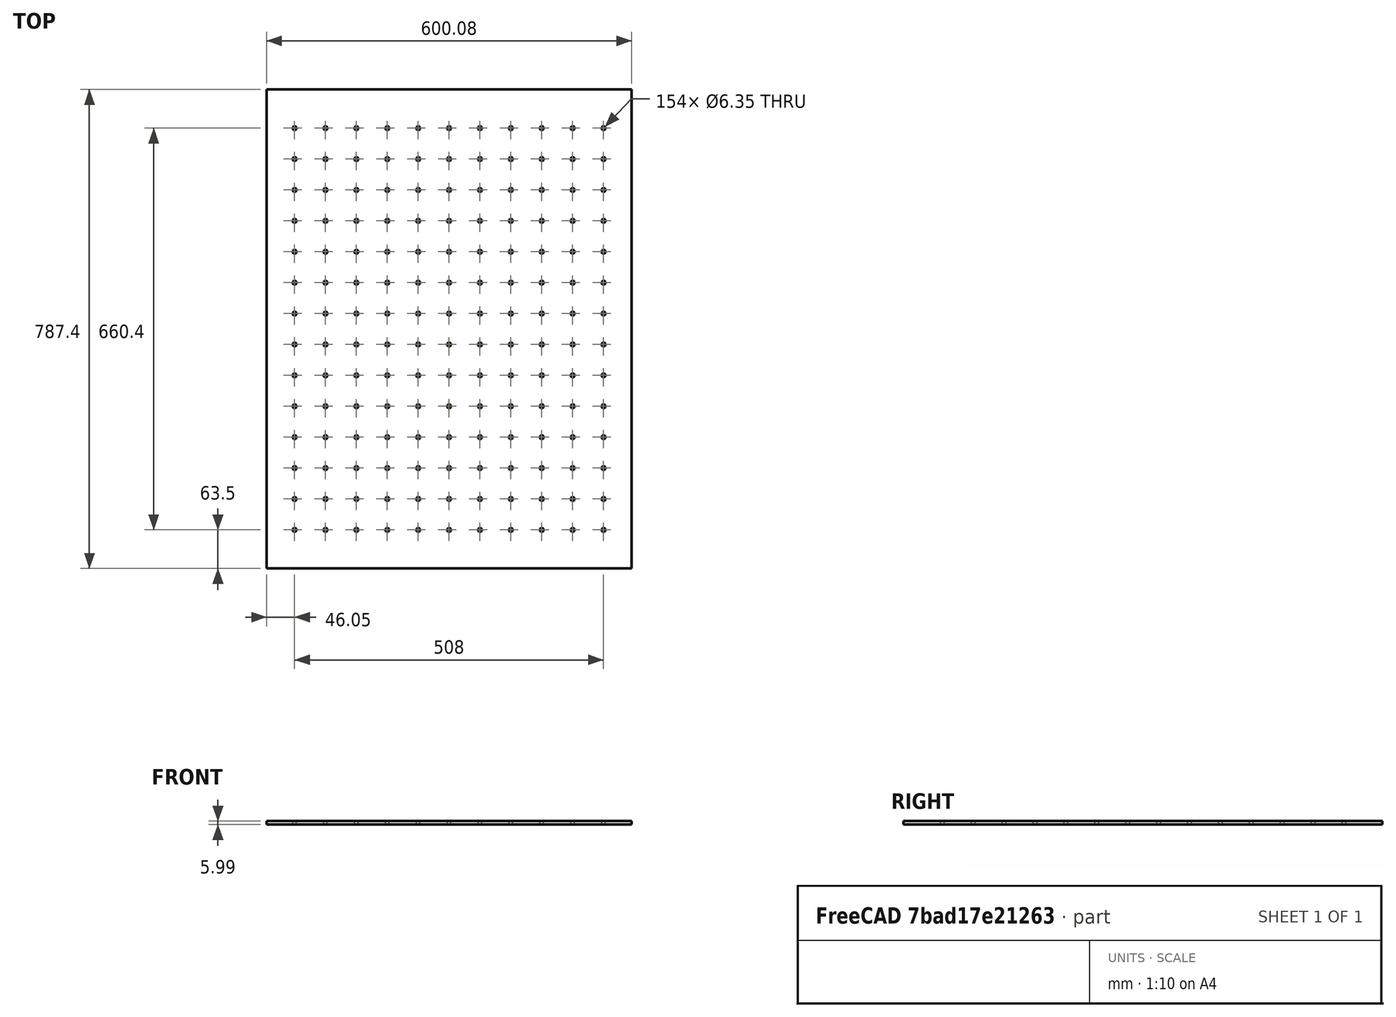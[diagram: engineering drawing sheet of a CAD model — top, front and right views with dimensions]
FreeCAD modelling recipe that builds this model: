
FCSTD DOCUMENT  (FreeCAD 0.19R24267 (Git))
Label: Inv2-P6
License: All rights reserved
LicenseURL: http://en.wikipedia.org/wiki/All_rights_reserved
objects: TechDraw::DrawViewDimension×8, TechDraw::DrawViewAnnotation×3, TechDraw::DrawProjGroupItem×2, TechDraw::DrawHatch×2, Sketcher::SketchObject×1, Part::Extrusion×1, TechDraw::DrawSVGTemplate×1, TechDraw::DrawProjGroup×1, TechDraw::DrawPage×1
note: 2 computed .brp shape members not serialized (recipe doc carries the construction recipe); baked Part::Feature solids carry a one-line shape summary decoded from their .brp

FEATURE [Sketcher::SketchObject] Sketch
  FullyConstrained = true
  sketch-geometry (311):
    g0: LineSegment StartX=0 StartY=0 StartZ=0 EndX=600.075 EndY=0 EndZ=0
    g1: LineSegment StartX=600.075 StartY=0 StartZ=0 EndX=600.075 EndY=-787.4 EndZ=0
    g2: LineSegment StartX=600.075 StartY=-787.4 StartZ=0 EndX=0 EndY=-787.4 EndZ=0
    g3: LineSegment StartX=0 StartY=-787.4 StartZ=0 EndX=0 EndY=0 EndZ=0
    g4: Circle CenterX=46.0502 CenterY=-63.5 CenterZ=0 NormalX=0 NormalY=0 NormalZ=1 AngleXU=0 Radius=3.175
    g5: Circle CenterX=96.8502 CenterY=-63.5 CenterZ=0 NormalX=0 NormalY=0 NormalZ=1 AngleXU=0 Radius=3.175
    g6: LineSegment StartX=46.0502 StartY=-63.5 StartZ=0 EndX=96.8502 EndY=-63.5 EndZ=0
    g7: Circle CenterX=147.65 CenterY=-63.5 CenterZ=0 NormalX=0 NormalY=0 NormalZ=1 AngleXU=0 Radius=3.175
    g8: LineSegment StartX=96.8502 StartY=-63.5 StartZ=0 EndX=147.65 EndY=-63.5 EndZ=0
    g9: Circle CenterX=198.45 CenterY=-63.5 CenterZ=0 NormalX=0 NormalY=0 NormalZ=1 AngleXU=0 Radius=3.175
    g10: LineSegment StartX=147.65 StartY=-63.5 StartZ=0 EndX=198.45 EndY=-63.5 EndZ=0
    g11: Circle CenterX=249.25 CenterY=-63.5 CenterZ=0 NormalX=0 NormalY=0 NormalZ=1 AngleXU=0 Radius=3.175
    g12: LineSegment StartX=198.45 StartY=-63.5 StartZ=0 EndX=249.25 EndY=-63.5 EndZ=0
    g13: Circle CenterX=300.05 CenterY=-63.5 CenterZ=0 NormalX=0 NormalY=0 NormalZ=1 AngleXU=0 Radius=3.175
    g14: LineSegment StartX=249.25 StartY=-63.5 StartZ=0 EndX=300.05 EndY=-63.5 EndZ=0
    g15: Circle CenterX=350.85 CenterY=-63.5 CenterZ=0 NormalX=0 NormalY=0 NormalZ=1 AngleXU=0 Radius=3.175
    g16: LineSegment StartX=300.05 StartY=-63.5 StartZ=0 EndX=350.85 EndY=-63.5 EndZ=0
    g17: Circle CenterX=401.65 CenterY=-63.5 CenterZ=0 NormalX=0 NormalY=0 NormalZ=1 AngleXU=0 Radius=3.175
    g18: LineSegment StartX=350.85 StartY=-63.5 StartZ=0 EndX=401.65 EndY=-63.5 EndZ=0
    g19: Circle CenterX=452.45 CenterY=-63.5 CenterZ=0 NormalX=0 NormalY=0 NormalZ=1 AngleXU=0 Radius=3.175
    g20: LineSegment StartX=401.65 StartY=-63.5 StartZ=0 EndX=452.45 EndY=-63.5 EndZ=0
    g21: Circle CenterX=503.25 CenterY=-63.5 CenterZ=0 NormalX=0 NormalY=0 NormalZ=1 AngleXU=0 Radius=3.175
    g22: LineSegment StartX=452.45 StartY=-63.5 StartZ=0 EndX=503.25 EndY=-63.5 EndZ=0
    g23: Circle CenterX=554.05 CenterY=-63.5 CenterZ=0 NormalX=0 NormalY=0 NormalZ=1 AngleXU=0 Radius=3.175
    g24: LineSegment StartX=503.25 StartY=-63.5 StartZ=0 EndX=554.05 EndY=-63.5 EndZ=0
    g25: Circle CenterX=46.0502 CenterY=-114.3 CenterZ=0 NormalX=0 NormalY=0 NormalZ=1 AngleXU=0 Radius=3.175
    g26: LineSegment StartX=46.0502 StartY=-63.5 StartZ=0 EndX=46.0502 EndY=-114.3 EndZ=0
    g27: Circle CenterX=96.8502 CenterY=-114.3 CenterZ=0 NormalX=0 NormalY=0 NormalZ=1 AngleXU=0 Radius=3.175
    g28: LineSegment StartX=46.0502 StartY=-114.3 StartZ=0 EndX=96.8502 EndY=-114.3 EndZ=0
    g29: Circle CenterX=147.65 CenterY=-114.3 CenterZ=0 NormalX=0 NormalY=0 NormalZ=1 AngleXU=0 Radius=3.175
    g30: LineSegment StartX=96.8502 StartY=-114.3 StartZ=0 EndX=147.65 EndY=-114.3 EndZ=0
    g31: Circle CenterX=198.45 CenterY=-114.3 CenterZ=0 NormalX=0 NormalY=0 NormalZ=1 AngleXU=0 Radius=3.175
    g32: LineSegment StartX=147.65 StartY=-114.3 StartZ=0 EndX=198.45 EndY=-114.3 EndZ=0
    g33: Circle CenterX=249.25 CenterY=-114.3 CenterZ=0 NormalX=0 NormalY=0 NormalZ=1 AngleXU=0 Radius=3.175
    g34: LineSegment StartX=198.45 StartY=-114.3 StartZ=0 EndX=249.25 EndY=-114.3 EndZ=0
    g35: Circle CenterX=300.05 CenterY=-114.3 CenterZ=0 NormalX=0 NormalY=0 NormalZ=1 AngleXU=0 Radius=3.175
    g36: LineSegment StartX=249.25 StartY=-114.3 StartZ=0 EndX=300.05 EndY=-114.3 EndZ=0
    g37: Circle CenterX=350.85 CenterY=-114.3 CenterZ=0 NormalX=0 NormalY=0 NormalZ=1 AngleXU=0 Radius=3.175
    g38: LineSegment StartX=300.05 StartY=-114.3 StartZ=0 EndX=350.85 EndY=-114.3 EndZ=0
    g39: Circle CenterX=401.65 CenterY=-114.3 CenterZ=0 NormalX=0 NormalY=0 NormalZ=1 AngleXU=0 Radius=3.175
    g40: LineSegment StartX=350.85 StartY=-114.3 StartZ=0 EndX=401.65 EndY=-114.3 EndZ=0
    g41: Circle CenterX=452.45 CenterY=-114.3 CenterZ=0 NormalX=0 NormalY=0 NormalZ=1 AngleXU=0 Radius=3.175
    g42: LineSegment StartX=401.65 StartY=-114.3 StartZ=0 EndX=452.45 EndY=-114.3 EndZ=0
    g43: Circle CenterX=503.25 CenterY=-114.3 CenterZ=0 NormalX=0 NormalY=0 NormalZ=1 AngleXU=0 Radius=3.175
    g44: LineSegment StartX=452.45 StartY=-114.3 StartZ=0 EndX=503.25 EndY=-114.3 EndZ=0
    g45: Circle CenterX=554.05 CenterY=-114.3 CenterZ=0 NormalX=0 NormalY=0 NormalZ=1 AngleXU=0 Radius=3.175
    g46: LineSegment StartX=503.25 StartY=-114.3 StartZ=0 EndX=554.05 EndY=-114.3 EndZ=0
    g47: Circle CenterX=46.0502 CenterY=-165.1 CenterZ=0 NormalX=0 NormalY=0 NormalZ=1 AngleXU=0 Radius=3.175
    g48: LineSegment StartX=46.0502 StartY=-114.3 StartZ=0 EndX=46.0502 EndY=-165.1 EndZ=0
    g49: Circle CenterX=96.8502 CenterY=-165.1 CenterZ=0 NormalX=0 NormalY=0 NormalZ=1 AngleXU=0 Radius=3.175
    g50: LineSegment StartX=46.0502 StartY=-165.1 StartZ=0 EndX=96.8502 EndY=-165.1 EndZ=0
    g51: Circle CenterX=147.65 CenterY=-165.1 CenterZ=0 NormalX=0 NormalY=0 NormalZ=1 AngleXU=0 Radius=3.175
    g52: LineSegment StartX=96.8502 StartY=-165.1 StartZ=0 EndX=147.65 EndY=-165.1 EndZ=0
    g53: Circle CenterX=198.45 CenterY=-165.1 CenterZ=0 NormalX=0 NormalY=0 NormalZ=1 AngleXU=0 Radius=3.175
    g54: LineSegment StartX=147.65 StartY=-165.1 StartZ=0 EndX=198.45 EndY=-165.1 EndZ=0
    g55: Circle CenterX=249.25 CenterY=-165.1 CenterZ=0 NormalX=0 NormalY=0 NormalZ=1 AngleXU=0 Radius=3.175
    g56: LineSegment StartX=198.45 StartY=-165.1 StartZ=0 EndX=249.25 EndY=-165.1 EndZ=0
    g57: Circle CenterX=300.05 CenterY=-165.1 CenterZ=0 NormalX=0 NormalY=0 NormalZ=1 AngleXU=0 Radius=3.175
    g58: LineSegment StartX=249.25 StartY=-165.1 StartZ=0 EndX=300.05 EndY=-165.1 EndZ=0
    g59: Circle CenterX=350.85 CenterY=-165.1 CenterZ=0 NormalX=0 NormalY=0 NormalZ=1 AngleXU=0 Radius=3.175
    g60: LineSegment StartX=300.05 StartY=-165.1 StartZ=0 EndX=350.85 EndY=-165.1 EndZ=0
    g61: Circle CenterX=401.65 CenterY=-165.1 CenterZ=0 NormalX=0 NormalY=0 NormalZ=1 AngleXU=0 Radius=3.175
    g62: LineSegment StartX=350.85 StartY=-165.1 StartZ=0 EndX=401.65 EndY=-165.1 EndZ=0
    g63: Circle CenterX=452.45 CenterY=-165.1 CenterZ=0 NormalX=0 NormalY=0 NormalZ=1 AngleXU=0 Radius=3.175
    g64: LineSegment StartX=401.65 StartY=-165.1 StartZ=0 EndX=452.45 EndY=-165.1 EndZ=0
    g65: Circle CenterX=503.25 CenterY=-165.1 CenterZ=0 NormalX=0 NormalY=0 NormalZ=1 AngleXU=0 Radius=3.175
    g66: LineSegment StartX=452.45 StartY=-165.1 StartZ=0 EndX=503.25 EndY=-165.1 EndZ=0
    g67: Circle CenterX=554.05 CenterY=-165.1 CenterZ=0 NormalX=0 NormalY=0 NormalZ=1 AngleXU=0 Radius=3.175
    g68: LineSegment StartX=503.25 StartY=-165.1 StartZ=0 EndX=554.05 EndY=-165.1 EndZ=0
    g69: Circle CenterX=46.0502 CenterY=-215.9 CenterZ=0 NormalX=0 NormalY=0 NormalZ=1 AngleXU=0 Radius=3.175
    g70: LineSegment StartX=46.0502 StartY=-165.1 StartZ=0 EndX=46.0502 EndY=-215.9 EndZ=0
    g71: Circle CenterX=96.8502 CenterY=-215.9 CenterZ=0 NormalX=0 NormalY=0 NormalZ=1 AngleXU=0 Radius=3.175
    g72: LineSegment StartX=46.0502 StartY=-215.9 StartZ=0 EndX=96.8502 EndY=-215.9 EndZ=0
    g73: Circle CenterX=147.65 CenterY=-215.9 CenterZ=0 NormalX=0 NormalY=0 NormalZ=1 AngleXU=0 Radius=3.175
    g74: LineSegment StartX=96.8502 StartY=-215.9 StartZ=0 EndX=147.65 EndY=-215.9 EndZ=0
    g75: Circle CenterX=198.45 CenterY=-215.9 CenterZ=0 NormalX=0 NormalY=0 NormalZ=1 AngleXU=0 Radius=3.175
    g76: LineSegment StartX=147.65 StartY=-215.9 StartZ=0 EndX=198.45 EndY=-215.9 EndZ=0
    g77: Circle CenterX=249.25 CenterY=-215.9 CenterZ=0 NormalX=0 NormalY=0 NormalZ=1 AngleXU=0 Radius=3.175
    g78: LineSegment StartX=198.45 StartY=-215.9 StartZ=0 EndX=249.25 EndY=-215.9 EndZ=0
    g79: Circle CenterX=300.05 CenterY=-215.9 CenterZ=0 NormalX=0 NormalY=0 NormalZ=1 AngleXU=0 Radius=3.175
    g80: LineSegment StartX=249.25 StartY=-215.9 StartZ=0 EndX=300.05 EndY=-215.9 EndZ=0
    g81: Circle CenterX=350.85 CenterY=-215.9 CenterZ=0 NormalX=0 NormalY=0 NormalZ=1 AngleXU=0 Radius=3.175
    g82: LineSegment StartX=300.05 StartY=-215.9 StartZ=0 EndX=350.85 EndY=-215.9 EndZ=0
    g83: Circle CenterX=401.65 CenterY=-215.9 CenterZ=0 NormalX=0 NormalY=0 NormalZ=1 AngleXU=0 Radius=3.175
    g84: LineSegment StartX=350.85 StartY=-215.9 StartZ=0 EndX=401.65 EndY=-215.9 EndZ=0
    g85: Circle CenterX=452.45 CenterY=-215.9 CenterZ=0 NormalX=0 NormalY=0 NormalZ=1 AngleXU=0 Radius=3.175
    g86: LineSegment StartX=401.65 StartY=-215.9 StartZ=0 EndX=452.45 EndY=-215.9 EndZ=0
    g87: Circle CenterX=503.25 CenterY=-215.9 CenterZ=0 NormalX=0 NormalY=0 NormalZ=1 AngleXU=0 Radius=3.175
    g88: LineSegment StartX=452.45 StartY=-215.9 StartZ=0 EndX=503.25 EndY=-215.9 EndZ=0
    g89: Circle CenterX=554.05 CenterY=-215.9 CenterZ=0 NormalX=0 NormalY=0 NormalZ=1 AngleXU=0 Radius=3.175
    g90: LineSegment StartX=503.25 StartY=-215.9 StartZ=0 EndX=554.05 EndY=-215.9 EndZ=0
    g91: Circle CenterX=46.0502 CenterY=-266.7 CenterZ=0 NormalX=0 NormalY=0 NormalZ=1 AngleXU=0 Radius=3.175
    g92: LineSegment StartX=46.0502 StartY=-215.9 StartZ=0 EndX=46.0502 EndY=-266.7 EndZ=0
    g93: Circle CenterX=96.8502 CenterY=-266.7 CenterZ=0 NormalX=0 NormalY=0 NormalZ=1 AngleXU=0 Radius=3.175
    g94: LineSegment StartX=46.0502 StartY=-266.7 StartZ=0 EndX=96.8502 EndY=-266.7 EndZ=0
    g95: Circle CenterX=147.65 CenterY=-266.7 CenterZ=0 NormalX=0 NormalY=0 NormalZ=1 AngleXU=0 Radius=3.175
    g96: LineSegment StartX=96.8502 StartY=-266.7 StartZ=0 EndX=147.65 EndY=-266.7 EndZ=0
    g97: Circle CenterX=198.45 CenterY=-266.7 CenterZ=0 NormalX=0 NormalY=0 NormalZ=1 AngleXU=0 Radius=3.175
    g98: LineSegment StartX=147.65 StartY=-266.7 StartZ=0 EndX=198.45 EndY=-266.7 EndZ=0
    g99: Circle CenterX=249.25 CenterY=-266.7 CenterZ=0 NormalX=0 NormalY=0 NormalZ=1 AngleXU=0 Radius=3.175
    g100: LineSegment StartX=198.45 StartY=-266.7 StartZ=0 EndX=249.25 EndY=-266.7 EndZ=0
    g101: Circle CenterX=300.05 CenterY=-266.7 CenterZ=0 NormalX=0 NormalY=0 NormalZ=1 AngleXU=0 Radius=3.175
    g102: LineSegment StartX=249.25 StartY=-266.7 StartZ=0 EndX=300.05 EndY=-266.7 EndZ=0
    g103: Circle CenterX=350.85 CenterY=-266.7 CenterZ=0 NormalX=0 NormalY=0 NormalZ=1 AngleXU=0 Radius=3.175
    g104: LineSegment StartX=300.05 StartY=-266.7 StartZ=0 EndX=350.85 EndY=-266.7 EndZ=0
    g105: Circle CenterX=401.65 CenterY=-266.7 CenterZ=0 NormalX=0 NormalY=0 NormalZ=1 AngleXU=0 Radius=3.175
    g106: LineSegment StartX=350.85 StartY=-266.7 StartZ=0 EndX=401.65 EndY=-266.7 EndZ=0
    g107: Circle CenterX=452.45 CenterY=-266.7 CenterZ=0 NormalX=0 NormalY=0 NormalZ=1 AngleXU=0 Radius=3.175
    g108: LineSegment StartX=401.65 StartY=-266.7 StartZ=0 EndX=452.45 EndY=-266.7 EndZ=0
    g109: Circle CenterX=503.25 CenterY=-266.7 CenterZ=0 NormalX=0 NormalY=0 NormalZ=1 AngleXU=0 Radius=3.175
    g110: LineSegment StartX=452.45 StartY=-266.7 StartZ=0 EndX=503.25 EndY=-266.7 EndZ=0
    g111: Circle CenterX=554.05 CenterY=-266.7 CenterZ=0 NormalX=0 NormalY=0 NormalZ=1 AngleXU=0 Radius=3.175
    g112: LineSegment StartX=503.25 StartY=-266.7 StartZ=0 EndX=554.05 EndY=-266.7 EndZ=0
    g113: Circle CenterX=46.0502 CenterY=-317.5 CenterZ=0 NormalX=0 NormalY=0 NormalZ=1 AngleXU=0 Radius=3.175
    g114: LineSegment StartX=46.0502 StartY=-266.7 StartZ=0 EndX=46.0502 EndY=-317.5 EndZ=0
    g115: Circle CenterX=96.8502 CenterY=-317.5 CenterZ=0 NormalX=0 NormalY=0 NormalZ=1 AngleXU=0 Radius=3.175
    g116: LineSegment StartX=46.0502 StartY=-317.5 StartZ=0 EndX=96.8502 EndY=-317.5 EndZ=0
    g117: Circle CenterX=147.65 CenterY=-317.5 CenterZ=0 NormalX=0 NormalY=0 NormalZ=1 AngleXU=0 Radius=3.175
    g118: LineSegment StartX=96.8502 StartY=-317.5 StartZ=0 EndX=147.65 EndY=-317.5 EndZ=0
    g119: Circle CenterX=198.45 CenterY=-317.5 CenterZ=0 NormalX=0 NormalY=0 NormalZ=1 AngleXU=0 Radius=3.175
    g120: LineSegment StartX=147.65 StartY=-317.5 StartZ=0 EndX=198.45 EndY=-317.5 EndZ=0
    g121: Circle CenterX=249.25 CenterY=-317.5 CenterZ=0 NormalX=0 NormalY=0 NormalZ=1 AngleXU=0 Radius=3.175
    g122: LineSegment StartX=198.45 StartY=-317.5 StartZ=0 EndX=249.25 EndY=-317.5 EndZ=0
    g123: Circle CenterX=300.05 CenterY=-317.5 CenterZ=0 NormalX=0 NormalY=0 NormalZ=1 AngleXU=0 Radius=3.175
    g124: LineSegment StartX=249.25 StartY=-317.5 StartZ=0 EndX=300.05 EndY=-317.5 EndZ=0
    g125: Circle CenterX=350.85 CenterY=-317.5 CenterZ=0 NormalX=0 NormalY=0 NormalZ=1 AngleXU=0 Radius=3.175
    g126: LineSegment StartX=300.05 StartY=-317.5 StartZ=0 EndX=350.85 EndY=-317.5 EndZ=0
    g127: Circle CenterX=401.65 CenterY=-317.5 CenterZ=0 NormalX=0 NormalY=0 NormalZ=1 AngleXU=0 Radius=3.175
    g128: LineSegment StartX=350.85 StartY=-317.5 StartZ=0 EndX=401.65 EndY=-317.5 EndZ=0
    g129: Circle CenterX=452.45 CenterY=-317.5 CenterZ=0 NormalX=0 NormalY=0 NormalZ=1 AngleXU=0 Radius=3.175
    g130: LineSegment StartX=401.65 StartY=-317.5 StartZ=0 EndX=452.45 EndY=-317.5 EndZ=0
    g131: Circle CenterX=503.25 CenterY=-317.5 CenterZ=0 NormalX=0 NormalY=0 NormalZ=1 AngleXU=0 Radius=3.175
    g132: LineSegment StartX=452.45 StartY=-317.5 StartZ=0 EndX=503.25 EndY=-317.5 EndZ=0
    g133: Circle CenterX=554.05 CenterY=-317.5 CenterZ=0 NormalX=0 NormalY=0 NormalZ=1 AngleXU=0 Radius=3.175
    g134: LineSegment StartX=503.25 StartY=-317.5 StartZ=0 EndX=554.05 EndY=-317.5 EndZ=0
    g135: Circle CenterX=46.0502 CenterY=-368.3 CenterZ=0 NormalX=0 NormalY=0 NormalZ=1 AngleXU=0 Radius=3.175
    g136: LineSegment StartX=46.0502 StartY=-317.5 StartZ=0 EndX=46.0502 EndY=-368.3 EndZ=0
    g137: Circle CenterX=96.8502 CenterY=-368.3 CenterZ=0 NormalX=0 NormalY=0 NormalZ=1 AngleXU=0 Radius=3.175
    g138: LineSegment StartX=46.0502 StartY=-368.3 StartZ=0 EndX=96.8502 EndY=-368.3 EndZ=0
    g139: Circle CenterX=147.65 CenterY=-368.3 CenterZ=0 NormalX=0 NormalY=0 NormalZ=1 AngleXU=0 Radius=3.175
    g140: LineSegment StartX=96.8502 StartY=-368.3 StartZ=0 EndX=147.65 EndY=-368.3 EndZ=0
    g141: Circle CenterX=198.45 CenterY=-368.3 CenterZ=0 NormalX=0 NormalY=0 NormalZ=1 AngleXU=0 Radius=3.175
    g142: LineSegment StartX=147.65 StartY=-368.3 StartZ=0 EndX=198.45 EndY=-368.3 EndZ=0
    g143: Circle CenterX=249.25 CenterY=-368.3 CenterZ=0 NormalX=0 NormalY=0 NormalZ=1 AngleXU=0 Radius=3.175
    g144: LineSegment StartX=198.45 StartY=-368.3 StartZ=0 EndX=249.25 EndY=-368.3 EndZ=0
    g145: Circle CenterX=300.05 CenterY=-368.3 CenterZ=0 NormalX=0 NormalY=0 NormalZ=1 AngleXU=0 Radius=3.175
    g146: LineSegment StartX=249.25 StartY=-368.3 StartZ=0 EndX=300.05 EndY=-368.3 EndZ=0
    g147: Circle CenterX=350.85 CenterY=-368.3 CenterZ=0 NormalX=0 NormalY=0 NormalZ=1 AngleXU=0 Radius=3.175
    g148: LineSegment StartX=300.05 StartY=-368.3 StartZ=0 EndX=350.85 EndY=-368.3 EndZ=0
    g149: Circle CenterX=401.65 CenterY=-368.3 CenterZ=0 NormalX=0 NormalY=0 NormalZ=1 AngleXU=0 Radius=3.175
    g150: LineSegment StartX=350.85 StartY=-368.3 StartZ=0 EndX=401.65 EndY=-368.3 EndZ=0
    g151: Circle CenterX=452.45 CenterY=-368.3 CenterZ=0 NormalX=0 NormalY=0 NormalZ=1 AngleXU=0 Radius=3.175
    g152: LineSegment StartX=401.65 StartY=-368.3 StartZ=0 EndX=452.45 EndY=-368.3 EndZ=0
    g153: Circle CenterX=503.25 CenterY=-368.3 CenterZ=0 NormalX=0 NormalY=0 NormalZ=1 AngleXU=0 Radius=3.175
    g154: LineSegment StartX=452.45 StartY=-368.3 StartZ=0 EndX=503.25 EndY=-368.3 EndZ=0
    g155: Circle CenterX=554.05 CenterY=-368.3 CenterZ=0 NormalX=0 NormalY=0 NormalZ=1 AngleXU=0 Radius=3.175
    g156: LineSegment StartX=503.25 StartY=-368.3 StartZ=0 EndX=554.05 EndY=-368.3 EndZ=0
    g157: Circle CenterX=46.0502 CenterY=-419.1 CenterZ=0 NormalX=0 NormalY=0 NormalZ=1 AngleXU=0 Radius=3.175
    g158: LineSegment StartX=46.0502 StartY=-368.3 StartZ=0 EndX=46.0502 EndY=-419.1 EndZ=0
    g159: Circle CenterX=96.8502 CenterY=-419.1 CenterZ=0 NormalX=0 NormalY=0 NormalZ=1 AngleXU=0 Radius=3.175
    g160: LineSegment StartX=46.0502 StartY=-419.1 StartZ=0 EndX=96.8502 EndY=-419.1 EndZ=0
    g161: Circle CenterX=147.65 CenterY=-419.1 CenterZ=0 NormalX=0 NormalY=0 NormalZ=1 AngleXU=0 Radius=3.175
    g162: LineSegment StartX=96.8502 StartY=-419.1 StartZ=0 EndX=147.65 EndY=-419.1 EndZ=0
    g163: Circle CenterX=198.45 CenterY=-419.1 CenterZ=0 NormalX=0 NormalY=0 NormalZ=1 AngleXU=0 Radius=3.175
    g164: LineSegment StartX=147.65 StartY=-419.1 StartZ=0 EndX=198.45 EndY=-419.1 EndZ=0
    g165: Circle CenterX=249.25 CenterY=-419.1 CenterZ=0 NormalX=0 NormalY=0 NormalZ=1 AngleXU=0 Radius=3.175
    g166: LineSegment StartX=198.45 StartY=-419.1 StartZ=0 EndX=249.25 EndY=-419.1 EndZ=0
    g167: Circle CenterX=300.05 CenterY=-419.1 CenterZ=0 NormalX=0 NormalY=0 NormalZ=1 AngleXU=0 Radius=3.175
    g168: LineSegment StartX=249.25 StartY=-419.1 StartZ=0 EndX=300.05 EndY=-419.1 EndZ=0
    g169: Circle CenterX=350.85 CenterY=-419.1 CenterZ=0 NormalX=0 NormalY=0 NormalZ=1 AngleXU=0 Radius=3.175
    g170: LineSegment StartX=300.05 StartY=-419.1 StartZ=0 EndX=350.85 EndY=-419.1 EndZ=0
    g171: Circle CenterX=401.65 CenterY=-419.1 CenterZ=0 NormalX=0 NormalY=0 NormalZ=1 AngleXU=0 Radius=3.175
    g172: LineSegment StartX=350.85 StartY=-419.1 StartZ=0 EndX=401.65 EndY=-419.1 EndZ=0
    g173: Circle CenterX=452.45 CenterY=-419.1 CenterZ=0 NormalX=0 NormalY=0 NormalZ=1 AngleXU=0 Radius=3.175
    g174: LineSegment StartX=401.65 StartY=-419.1 StartZ=0 EndX=452.45 EndY=-419.1 EndZ=0
    g175: Circle CenterX=503.25 CenterY=-419.1 CenterZ=0 NormalX=0 NormalY=0 NormalZ=1 AngleXU=0 Radius=3.175
    g176: LineSegment StartX=452.45 StartY=-419.1 StartZ=0 EndX=503.25 EndY=-419.1 EndZ=0
    g177: Circle CenterX=554.05 CenterY=-419.1 CenterZ=0 NormalX=0 NormalY=0 NormalZ=1 AngleXU=0 Radius=3.175
    g178: LineSegment StartX=503.25 StartY=-419.1 StartZ=0 EndX=554.05 EndY=-419.1 EndZ=0
    g179: Circle CenterX=46.0502 CenterY=-469.9 CenterZ=0 NormalX=0 NormalY=0 NormalZ=1 AngleXU=0 Radius=3.175
    g180: LineSegment StartX=46.0502 StartY=-419.1 StartZ=0 EndX=46.0502 EndY=-469.9 EndZ=0
    g181: Circle CenterX=96.8502 CenterY=-469.9 CenterZ=0 NormalX=0 NormalY=0 NormalZ=1 AngleXU=0 Radius=3.175
    g182: LineSegment StartX=46.0502 StartY=-469.9 StartZ=0 EndX=96.8502 EndY=-469.9 EndZ=0
    g183: Circle CenterX=147.65 CenterY=-469.9 CenterZ=0 NormalX=0 NormalY=0 NormalZ=1 AngleXU=0 Radius=3.175
    g184: LineSegment StartX=96.8502 StartY=-469.9 StartZ=0 EndX=147.65 EndY=-469.9 EndZ=0
    g185: Circle CenterX=198.45 CenterY=-469.9 CenterZ=0 NormalX=0 NormalY=0 NormalZ=1 AngleXU=0 Radius=3.175
    g186: LineSegment StartX=147.65 StartY=-469.9 StartZ=0 EndX=198.45 EndY=-469.9 EndZ=0
    g187: Circle CenterX=249.25 CenterY=-469.9 CenterZ=0 NormalX=0 NormalY=0 NormalZ=1 AngleXU=0 Radius=3.175
    g188: LineSegment StartX=198.45 StartY=-469.9 StartZ=0 EndX=249.25 EndY=-469.9 EndZ=0
    g189: Circle CenterX=300.05 CenterY=-469.9 CenterZ=0 NormalX=0 NormalY=0 NormalZ=1 AngleXU=0 Radius=3.175
    g190: LineSegment StartX=249.25 StartY=-469.9 StartZ=0 EndX=300.05 EndY=-469.9 EndZ=0
    g191: Circle CenterX=350.85 CenterY=-469.9 CenterZ=0 NormalX=0 NormalY=0 NormalZ=1 AngleXU=0 Radius=3.175
    g192: LineSegment StartX=300.05 StartY=-469.9 StartZ=0 EndX=350.85 EndY=-469.9 EndZ=0
    g193: Circle CenterX=401.65 CenterY=-469.9 CenterZ=0 NormalX=0 NormalY=0 NormalZ=1 AngleXU=0 Radius=3.175
    g194: LineSegment StartX=350.85 StartY=-469.9 StartZ=0 EndX=401.65 EndY=-469.9 EndZ=0
    g195: Circle CenterX=452.45 CenterY=-469.9 CenterZ=0 NormalX=0 NormalY=0 NormalZ=1 AngleXU=0 Radius=3.175
    g196: LineSegment StartX=401.65 StartY=-469.9 StartZ=0 EndX=452.45 EndY=-469.9 EndZ=0
    g197: Circle CenterX=503.25 CenterY=-469.9 CenterZ=0 NormalX=0 NormalY=0 NormalZ=1 AngleXU=0 Radius=3.175
    g198: LineSegment StartX=452.45 StartY=-469.9 StartZ=0 EndX=503.25 EndY=-469.9 EndZ=0
    g199: Circle CenterX=554.05 CenterY=-469.9 CenterZ=0 NormalX=0 NormalY=0 NormalZ=1 AngleXU=0 Radius=3.175
    g200: LineSegment StartX=503.25 StartY=-469.9 StartZ=0 EndX=554.05 EndY=-469.9 EndZ=0
    g201: Circle CenterX=46.0502 CenterY=-520.7 CenterZ=0 NormalX=0 NormalY=0 NormalZ=1 AngleXU=0 Radius=3.175
    g202: LineSegment StartX=46.0502 StartY=-469.9 StartZ=0 EndX=46.0502 EndY=-520.7 EndZ=0
    g203: Circle CenterX=96.8502 CenterY=-520.7 CenterZ=0 NormalX=0 NormalY=0 NormalZ=1 AngleXU=0 Radius=3.175
    g204: LineSegment StartX=46.0502 StartY=-520.7 StartZ=0 EndX=96.8502 EndY=-520.7 EndZ=0
    g205: Circle CenterX=147.65 CenterY=-520.7 CenterZ=0 NormalX=0 NormalY=0 NormalZ=1 AngleXU=0 Radius=3.175
    g206: LineSegment StartX=96.8502 StartY=-520.7 StartZ=0 EndX=147.65 EndY=-520.7 EndZ=0
    g207: Circle CenterX=198.45 CenterY=-520.7 CenterZ=0 NormalX=0 NormalY=0 NormalZ=1 AngleXU=0 Radius=3.175
    g208: LineSegment StartX=147.65 StartY=-520.7 StartZ=0 EndX=198.45 EndY=-520.7 EndZ=0
    g209: Circle CenterX=249.25 CenterY=-520.7 CenterZ=0 NormalX=0 NormalY=0 NormalZ=1 AngleXU=0 Radius=3.175
    g210: LineSegment StartX=198.45 StartY=-520.7 StartZ=0 EndX=249.25 EndY=-520.7 EndZ=0
    g211: Circle CenterX=300.05 CenterY=-520.7 CenterZ=0 NormalX=0 NormalY=0 NormalZ=1 AngleXU=0 Radius=3.175
    g212: LineSegment StartX=249.25 StartY=-520.7 StartZ=0 EndX=300.05 EndY=-520.7 EndZ=0
    g213: Circle CenterX=350.85 CenterY=-520.7 CenterZ=0 NormalX=0 NormalY=0 NormalZ=1 AngleXU=0 Radius=3.175
    g214: LineSegment StartX=300.05 StartY=-520.7 StartZ=0 EndX=350.85 EndY=-520.7 EndZ=0
    g215: Circle CenterX=401.65 CenterY=-520.7 CenterZ=0 NormalX=0 NormalY=0 NormalZ=1 AngleXU=0 Radius=3.175
    g216: LineSegment StartX=350.85 StartY=-520.7 StartZ=0 EndX=401.65 EndY=-520.7 EndZ=0
    g217: Circle CenterX=452.45 CenterY=-520.7 CenterZ=0 NormalX=0 NormalY=0 NormalZ=1 AngleXU=0 Radius=3.175
    g218: LineSegment StartX=401.65 StartY=-520.7 StartZ=0 EndX=452.45 EndY=-520.7 EndZ=0
    g219: Circle CenterX=503.25 CenterY=-520.7 CenterZ=0 NormalX=0 NormalY=0 NormalZ=1 AngleXU=0 Radius=3.175
    g220: LineSegment StartX=452.45 StartY=-520.7 StartZ=0 EndX=503.25 EndY=-520.7 EndZ=0
    g221: Circle CenterX=554.05 CenterY=-520.7 CenterZ=0 NormalX=0 NormalY=0 NormalZ=1 AngleXU=0 Radius=3.175
    g222: LineSegment StartX=503.25 StartY=-520.7 StartZ=0 EndX=554.05 EndY=-520.7 EndZ=0
    g223: Circle CenterX=46.0502 CenterY=-571.5 CenterZ=0 NormalX=0 NormalY=0 NormalZ=1 AngleXU=0 Radius=3.175
    g224: LineSegment StartX=46.0502 StartY=-520.7 StartZ=0 EndX=46.0502 EndY=-571.5 EndZ=0
    g225: Circle CenterX=96.8502 CenterY=-571.5 CenterZ=0 NormalX=0 NormalY=0 NormalZ=1 AngleXU=0 Radius=3.175
    g226: LineSegment StartX=46.0502 StartY=-571.5 StartZ=0 EndX=96.8502 EndY=-571.5 EndZ=0
    g227: Circle CenterX=147.65 CenterY=-571.5 CenterZ=0 NormalX=0 NormalY=0 NormalZ=1 AngleXU=0 Radius=3.175
    g228: LineSegment StartX=96.8502 StartY=-571.5 StartZ=0 EndX=147.65 EndY=-571.5 EndZ=0
    g229: Circle CenterX=198.45 CenterY=-571.5 CenterZ=0 NormalX=0 NormalY=0 NormalZ=1 AngleXU=0 Radius=3.175
    g230: LineSegment StartX=147.65 StartY=-571.5 StartZ=0 EndX=198.45 EndY=-571.5 EndZ=0
    g231: Circle CenterX=249.25 CenterY=-571.5 CenterZ=0 NormalX=0 NormalY=0 NormalZ=1 AngleXU=0 Radius=3.175
    g232: LineSegment StartX=198.45 StartY=-571.5 StartZ=0 EndX=249.25 EndY=-571.5 EndZ=0
    g233: Circle CenterX=300.05 CenterY=-571.5 CenterZ=0 NormalX=0 NormalY=0 NormalZ=1 AngleXU=0 Radius=3.175
    g234: LineSegment StartX=249.25 StartY=-571.5 StartZ=0 EndX=300.05 EndY=-571.5 EndZ=0
    g235: Circle CenterX=350.85 CenterY=-571.5 CenterZ=0 NormalX=0 NormalY=0 NormalZ=1 AngleXU=0 Radius=3.175
    g236: LineSegment StartX=300.05 StartY=-571.5 StartZ=0 EndX=350.85 EndY=-571.5 EndZ=0
    g237: Circle CenterX=401.65 CenterY=-571.5 CenterZ=0 NormalX=0 NormalY=0 NormalZ=1 AngleXU=0 Radius=3.175
    g238: LineSegment StartX=350.85 StartY=-571.5 StartZ=0 EndX=401.65 EndY=-571.5 EndZ=0
    g239: Circle CenterX=452.45 CenterY=-571.5 CenterZ=0 NormalX=0 NormalY=0 NormalZ=1 AngleXU=0 Radius=3.175
    g240: LineSegment StartX=401.65 StartY=-571.5 StartZ=0 EndX=452.45 EndY=-571.5 EndZ=0
    g241: Circle CenterX=503.25 CenterY=-571.5 CenterZ=0 NormalX=0 NormalY=0 NormalZ=1 AngleXU=0 Radius=3.175
    g242: LineSegment StartX=452.45 StartY=-571.5 StartZ=0 EndX=503.25 EndY=-571.5 EndZ=0
    g243: Circle CenterX=554.05 CenterY=-571.5 CenterZ=0 NormalX=0 NormalY=0 NormalZ=1 AngleXU=0 Radius=3.175
    g244: LineSegment StartX=503.25 StartY=-571.5 StartZ=0 EndX=554.05 EndY=-571.5 EndZ=0
    g245: Circle CenterX=46.0502 CenterY=-622.3 CenterZ=0 NormalX=0 NormalY=0 NormalZ=1 AngleXU=0 Radius=3.175
    g246: LineSegment StartX=46.0502 StartY=-571.5 StartZ=0 EndX=46.0502 EndY=-622.3 EndZ=0
    g247: Circle CenterX=96.8502 CenterY=-622.3 CenterZ=0 NormalX=0 NormalY=0 NormalZ=1 AngleXU=0 Radius=3.175
    g248: LineSegment StartX=46.0502 StartY=-622.3 StartZ=0 EndX=96.8502 EndY=-622.3 EndZ=0
    g249: Circle CenterX=147.65 CenterY=-622.3 CenterZ=0 NormalX=0 NormalY=0 NormalZ=1 AngleXU=0 Radius=3.175
    g250: LineSegment StartX=96.8502 StartY=-622.3 StartZ=0 EndX=147.65 EndY=-622.3 EndZ=0
    g251: Circle CenterX=198.45 CenterY=-622.3 CenterZ=0 NormalX=0 NormalY=0 NormalZ=1 AngleXU=0 Radius=3.175
    g252: LineSegment StartX=147.65 StartY=-622.3 StartZ=0 EndX=198.45 EndY=-622.3 EndZ=0
    g253: Circle CenterX=249.25 CenterY=-622.3 CenterZ=0 NormalX=0 NormalY=0 NormalZ=1 AngleXU=0 Radius=3.175
    g254: LineSegment StartX=198.45 StartY=-622.3 StartZ=0 EndX=249.25 EndY=-622.3 EndZ=0
    g255: Circle CenterX=300.05 CenterY=-622.3 CenterZ=0 NormalX=0 NormalY=0 NormalZ=1 AngleXU=0 Radius=3.175
    g256: LineSegment StartX=249.25 StartY=-622.3 StartZ=0 EndX=300.05 EndY=-622.3 EndZ=0
    g257: Circle CenterX=350.85 CenterY=-622.3 CenterZ=0 NormalX=0 NormalY=0 NormalZ=1 AngleXU=0 Radius=3.175
    g258: LineSegment StartX=300.05 StartY=-622.3 StartZ=0 EndX=350.85 EndY=-622.3 EndZ=0
    g259: Circle CenterX=401.65 CenterY=-622.3 CenterZ=0 NormalX=0 NormalY=0 NormalZ=1 AngleXU=0 Radius=3.175
    g260: LineSegment StartX=350.85 StartY=-622.3 StartZ=0 EndX=401.65 EndY=-622.3 EndZ=0
    g261: Circle CenterX=452.45 CenterY=-622.3 CenterZ=0 NormalX=0 NormalY=0 NormalZ=1 AngleXU=0 Radius=3.175
    g262: LineSegment StartX=401.65 StartY=-622.3 StartZ=0 EndX=452.45 EndY=-622.3 EndZ=0
    g263: Circle CenterX=503.25 CenterY=-622.3 CenterZ=0 NormalX=0 NormalY=0 NormalZ=1 AngleXU=0 Radius=3.175
    g264: LineSegment StartX=452.45 StartY=-622.3 StartZ=0 EndX=503.25 EndY=-622.3 EndZ=0
    g265: Circle CenterX=554.05 CenterY=-622.3 CenterZ=0 NormalX=0 NormalY=0 NormalZ=1 AngleXU=0 Radius=3.175
    g266: LineSegment StartX=503.25 StartY=-622.3 StartZ=0 EndX=554.05 EndY=-622.3 EndZ=0
    g267: Circle CenterX=46.0502 CenterY=-673.1 CenterZ=0 NormalX=0 NormalY=0 NormalZ=1 AngleXU=0 Radius=3.175
    g268: LineSegment StartX=46.0502 StartY=-622.3 StartZ=0 EndX=46.0502 EndY=-673.1 EndZ=0
    g269: Circle CenterX=96.8502 CenterY=-673.1 CenterZ=0 NormalX=0 NormalY=0 NormalZ=1 AngleXU=0 Radius=3.175
    g270: LineSegment StartX=46.0502 StartY=-673.1 StartZ=0 EndX=96.8502 EndY=-673.1 EndZ=0
    g271: Circle CenterX=147.65 CenterY=-673.1 CenterZ=0 NormalX=0 NormalY=0 NormalZ=1 AngleXU=0 Radius=3.175
    g272: LineSegment StartX=96.8502 StartY=-673.1 StartZ=0 EndX=147.65 EndY=-673.1 EndZ=0
    g273: Circle CenterX=198.45 CenterY=-673.1 CenterZ=0 NormalX=0 NormalY=0 NormalZ=1 AngleXU=0 Radius=3.175
    g274: LineSegment StartX=147.65 StartY=-673.1 StartZ=0 EndX=198.45 EndY=-673.1 EndZ=0
    g275: Circle CenterX=249.25 CenterY=-673.1 CenterZ=0 NormalX=0 NormalY=0 NormalZ=1 AngleXU=0 Radius=3.175
    g276: LineSegment StartX=198.45 StartY=-673.1 StartZ=0 EndX=249.25 EndY=-673.1 EndZ=0
    g277: Circle CenterX=300.05 CenterY=-673.1 CenterZ=0 NormalX=0 NormalY=0 NormalZ=1 AngleXU=0 Radius=3.175
    g278: LineSegment StartX=249.25 StartY=-673.1 StartZ=0 EndX=300.05 EndY=-673.1 EndZ=0
    g279: Circle CenterX=350.85 CenterY=-673.1 CenterZ=0 NormalX=0 NormalY=0 NormalZ=1 AngleXU=0 Radius=3.175
    g280: LineSegment StartX=300.05 StartY=-673.1 StartZ=0 EndX=350.85 EndY=-673.1 EndZ=0
    g281: Circle CenterX=401.65 CenterY=-673.1 CenterZ=0 NormalX=0 NormalY=0 NormalZ=1 AngleXU=0 Radius=3.175
    g282: LineSegment StartX=350.85 StartY=-673.1 StartZ=0 EndX=401.65 EndY=-673.1 EndZ=0
    g283: Circle CenterX=452.45 CenterY=-673.1 CenterZ=0 NormalX=0 NormalY=0 NormalZ=1 AngleXU=0 Radius=3.175
    g284: LineSegment StartX=401.65 StartY=-673.1 StartZ=0 EndX=452.45 EndY=-673.1 EndZ=0
    g285: Circle CenterX=503.25 CenterY=-673.1 CenterZ=0 NormalX=0 NormalY=0 NormalZ=1 AngleXU=0 Radius=3.175
    g286: LineSegment StartX=452.45 StartY=-673.1 StartZ=0 EndX=503.25 EndY=-673.1 EndZ=0
    g287: Circle CenterX=554.05 CenterY=-673.1 CenterZ=0 NormalX=0 NormalY=0 NormalZ=1 AngleXU=0 Radius=3.175
    g288: LineSegment StartX=503.25 StartY=-673.1 StartZ=0 EndX=554.05 EndY=-673.1 EndZ=0
    g289: Circle CenterX=46.0502 CenterY=-723.9 CenterZ=0 NormalX=0 NormalY=0 NormalZ=1 AngleXU=0 Radius=3.175
    g290: LineSegment StartX=46.0502 StartY=-673.1 StartZ=0 EndX=46.0502 EndY=-723.9 EndZ=0
    g291: Circle CenterX=96.8502 CenterY=-723.9 CenterZ=0 NormalX=0 NormalY=0 NormalZ=1 AngleXU=0 Radius=3.175
    g292: LineSegment StartX=46.0502 StartY=-723.9 StartZ=0 EndX=96.8502 EndY=-723.9 EndZ=0
    g293: Circle CenterX=147.65 CenterY=-723.9 CenterZ=0 NormalX=0 NormalY=0 NormalZ=1 AngleXU=0 Radius=3.175
    g294: LineSegment StartX=96.8502 StartY=-723.9 StartZ=0 EndX=147.65 EndY=-723.9 EndZ=0
    g295: Circle CenterX=198.45 CenterY=-723.9 CenterZ=0 NormalX=0 NormalY=0 NormalZ=1 AngleXU=0 Radius=3.175
    g296: LineSegment StartX=147.65 StartY=-723.9 StartZ=0 EndX=198.45 EndY=-723.9 EndZ=0
    g297: Circle CenterX=249.25 CenterY=-723.9 CenterZ=0 NormalX=0 NormalY=0 NormalZ=1 AngleXU=0 Radius=3.175
    g298: LineSegment StartX=198.45 StartY=-723.9 StartZ=0 EndX=249.25 EndY=-723.9 EndZ=0
    g299: Circle CenterX=300.05 CenterY=-723.9 CenterZ=0 NormalX=0 NormalY=0 NormalZ=1 AngleXU=0 Radius=3.175
    g300: LineSegment StartX=249.25 StartY=-723.9 StartZ=0 EndX=300.05 EndY=-723.9 EndZ=0
    g301: Circle CenterX=350.85 CenterY=-723.9 CenterZ=0 NormalX=0 NormalY=0 NormalZ=1 AngleXU=0 Radius=3.175
    g302: LineSegment StartX=300.05 StartY=-723.9 StartZ=0 EndX=350.85 EndY=-723.9 EndZ=0
    g303: Circle CenterX=401.65 CenterY=-723.9 CenterZ=0 NormalX=0 NormalY=0 NormalZ=1 AngleXU=0 Radius=3.175
    g304: LineSegment StartX=350.85 StartY=-723.9 StartZ=0 EndX=401.65 EndY=-723.9 EndZ=0
    g305: Circle CenterX=452.45 CenterY=-723.9 CenterZ=0 NormalX=0 NormalY=0 NormalZ=1 AngleXU=0 Radius=3.175
    g306: LineSegment StartX=401.65 StartY=-723.9 StartZ=0 EndX=452.45 EndY=-723.9 EndZ=0
    g307: Circle CenterX=503.25 CenterY=-723.9 CenterZ=0 NormalX=0 NormalY=0 NormalZ=1 AngleXU=0 Radius=3.175
    g308: LineSegment StartX=452.45 StartY=-723.9 StartZ=0 EndX=503.25 EndY=-723.9 EndZ=0
    g309: Circle CenterX=554.05 CenterY=-723.9 CenterZ=0 NormalX=0 NormalY=0 NormalZ=1 AngleXU=0 Radius=3.175
    g310: LineSegment StartX=503.25 StartY=-723.9 StartZ=0 EndX=554.05 EndY=-723.9 EndZ=0
  constraints (779):
    c: Coincident(g0,g1)
    c: Coincident(g1,g2)
    c: Coincident(g2,g3)
    c: Coincident(g3,g0)
    c: Horizontal(g0)
    c: Horizontal(g2)
    c: Vertical(g1)
    c: Vertical(g3)
    c: Coincident(g0,g-1)
    c: DistanceY(g3,g3) = 787.4
    c: DistanceX(g0,g0) = 600.075
    c: Diameter(g4) = 6.35
    c: Distance(g4,g3) = 46.0502
    c: Distance(g4,g0) = 63.5
    c: Diameter(g5) = 6.35
    c: Coincident(g4,g6)
    c: Coincident(g5,g6)
    c: Distance(g6) = 50.8
    c: Angle(g6) = 0
    c: Diameter(g7) = 6.35
    c: Coincident(g5,g8)
    c: Coincident(g7,g8)
    c: Equal(g6,g8)
    c: Parallel(g8,g6)
    c: Diameter(g9) = 6.35
    c: Coincident(g7,g10)
    c: Coincident(g9,g10)
    c: Equal(g6,g10)
    c: Parallel(g10,g6)
    c: Diameter(g11) = 6.35
    c: Coincident(g9,g12)
    c: Coincident(g11,g12)
    c: Equal(g6,g12)
    c: Parallel(g12,g6)
    c: Diameter(g13) = 6.35
    c: Coincident(g11,g14)
    c: Coincident(g13,g14)
    c: Equal(g6,g14)
    c: Parallel(g14,g6)
    c: Diameter(g15) = 6.35
    c: Coincident(g13,g16)
    c: Coincident(g15,g16)
    c: Equal(g6,g16)
    c: Parallel(g16,g6)
    c: Diameter(g17) = 6.35
    c: Coincident(g15,g18)
    c: Coincident(g17,g18)
    c: Equal(g6,g18)
    c: Parallel(g18,g6)
    c: Diameter(g19) = 6.35
    c: Coincident(g17,g20)
    c: Coincident(g19,g20)
    c: Equal(g6,g20)
    c: Parallel(g20,g6)
    c: Diameter(g21) = 6.35
    c: Coincident(g19,g22)
    c: Coincident(g21,g22)
    c: Equal(g6,g22)
    c: Parallel(g22,g6)
    c: Diameter(g23) = 6.35
    c: Coincident(g21,g24)
    c: Coincident(g23,g24)
    c: Equal(g6,g24)
    c: Parallel(g24,g6)
    c: Diameter(g25) = 6.35
    c: Coincident(g4,g26)
    c: Coincident(g25,g26)
    c: Equal(g26,g6)
    c: Perpendicular(g26,g6)
    c: Diameter(g27) = 6.35
    c: Coincident(g25,g28)
    c: Coincident(g27,g28)
    c: Equal(g6,g28)
    c: Parallel(g28,g6)
    c: Diameter(g29) = 6.35
    c: Coincident(g27,g30)
    c: Coincident(g29,g30)
    c: Equal(g6,g30)
    c: Parallel(g30,g6)
    c: Diameter(g31) = 6.35
    c: Coincident(g29,g32)
    c: Coincident(g31,g32)
    c: Equal(g6,g32)
    c: Parallel(g32,g6)
    c: Diameter(g33) = 6.35
    c: Coincident(g31,g34)
    c: Coincident(g33,g34)
    c: Equal(g6,g34)
    c: Parallel(g34,g6)
    c: Diameter(g35) = 6.35
    c: Coincident(g33,g36)
    c: Coincident(g35,g36)
    c: Equal(g6,g36)
    c: Parallel(g36,g6)
    c: Diameter(g37) = 6.35
    c: Coincident(g35,g38)
    c: Coincident(g37,g38)
    c: Equal(g6,g38)
    c: Parallel(g38,g6)
    c: Diameter(g39) = 6.35
    c: Coincident(g37,g40)
    c: Coincident(g39,g40)
    c: Equal(g6,g40)
    c: Parallel(g40,g6)
    c: Diameter(g41) = 6.35
    c: Coincident(g39,g42)
    c: Coincident(g41,g42)
    c: Equal(g6,g42)
    c: Parallel(g42,g6)
    c: Diameter(g43) = 6.35
    c: Coincident(g41,g44)
    c: Coincident(g43,g44)
    c: Equal(g6,g44)
    c: Parallel(g44,g6)
    c: Diameter(g45) = 6.35
    c: Coincident(g43,g46)
    c: Coincident(g45,g46)
    c: Equal(g6,g46)
    c: Parallel(g46,g6)
    c: Diameter(g47) = 6.35
    c: Coincident(g25,g48)
    c: Coincident(g47,g48)
    c: Equal(g26,g48)
    c: Perpendicular(g48,g6)
    c: Diameter(g49) = 6.35
    c: Coincident(g47,g50)
    c: Coincident(g49,g50)
    c: Equal(g6,g50)
    c: Parallel(g50,g6)
    c: Diameter(g51) = 6.35
    c: Coincident(g49,g52)
    c: Coincident(g51,g52)
    c: Equal(g6,g52)
    c: Parallel(g52,g6)
    c: Diameter(g53) = 6.35
    c: Coincident(g51,g54)
    c: Coincident(g53,g54)
    c: Equal(g6,g54)
    c: Parallel(g54,g6)
    c: Diameter(g55) = 6.35
    c: Coincident(g53,g56)
    c: Coincident(g55,g56)
    c: Equal(g6,g56)
    c: Parallel(g56,g6)
    c: Diameter(g57) = 6.35
    c: Coincident(g55,g58)
    c: Coincident(g57,g58)
    c: Equal(g6,g58)
    c: Parallel(g58,g6)
    c: Diameter(g59) = 6.35
    c: Coincident(g57,g60)
    c: Coincident(g59,g60)
    c: Equal(g6,g60)
    c: Parallel(g60,g6)
    c: Diameter(g61) = 6.35
    c: Coincident(g59,g62)
    c: Coincident(g61,g62)
    c: Equal(g6,g62)
    c: Parallel(g62,g6)
    c: Diameter(g63) = 6.35
    c: Coincident(g61,g64)
    c: Coincident(g63,g64)
    c: Equal(g6,g64)
    c: Parallel(g64,g6)
    c: Diameter(g65) = 6.35
    c: Coincident(g63,g66)
    c: Coincident(g65,g66)
    c: Equal(g6,g66)
    c: Parallel(g66,g6)
    c: Diameter(g67) = 6.35
    c: Coincident(g65,g68)
    c: Coincident(g67,g68)
    c: Equal(g6,g68)
    c: Parallel(g68,g6)
    c: Diameter(g69) = 6.35
    c: Coincident(g47,g70)
    c: Coincident(g69,g70)
    c: Equal(g26,g70)
    c: Perpendicular(g70,g6)
    c: Diameter(g71) = 6.35
    c: Coincident(g69,g72)
    c: Coincident(g71,g72)
    c: Equal(g6,g72)
    c: Parallel(g72,g6)
    c: Diameter(g73) = 6.35
    c: Coincident(g71,g74)
    c: Coincident(g73,g74)
    c: Equal(g6,g74)
    c: Parallel(g74,g6)
    c: Diameter(g75) = 6.35
    c: Coincident(g73,g76)
    c: Coincident(g75,g76)
    c: Equal(g6,g76)
    c: Parallel(g76,g6)
    c: Diameter(g77) = 6.35
    c: Coincident(g75,g78)
    c: Coincident(g77,g78)
    c: Equal(g6,g78)
    c: Parallel(g78,g6)
    c: Diameter(g79) = 6.35
    c: Coincident(g77,g80)
    c: Coincident(g79,g80)
    c: Equal(g6,g80)
    c: Parallel(g80,g6)
    c: Diameter(g81) = 6.35
    c: Coincident(g79,g82)
    c: Coincident(g81,g82)
    c: Equal(g6,g82)
    c: Parallel(g82,g6)
    c: Diameter(g83) = 6.35
    c: Coincident(g81,g84)
    c: Coincident(g83,g84)
    c: Equal(g6,g84)
    c: Parallel(g84,g6)
    c: Diameter(g85) = 6.35
    c: Coincident(g83,g86)
    c: Coincident(g85,g86)
    c: Equal(g6,g86)
    c: Parallel(g86,g6)
    c: Diameter(g87) = 6.35
    c: Coincident(g85,g88)
    c: Coincident(g87,g88)
    c: Equal(g6,g88)
    c: Parallel(g88,g6)
    c: Diameter(g89) = 6.35
    c: Coincident(g87,g90)
    c: Coincident(g89,g90)
    c: Equal(g6,g90)
    c: Parallel(g90,g6)
    c: Diameter(g91) = 6.35
    c: Coincident(g69,g92)
    c: Coincident(g91,g92)
    c: Equal(g26,g92)
    c: Perpendicular(g92,g6)
    c: Diameter(g93) = 6.35
    c: Coincident(g91,g94)
    c: Coincident(g93,g94)
    c: Equal(g6,g94)
    c: Parallel(g94,g6)
    c: Diameter(g95) = 6.35
    c: Coincident(g93,g96)
    c: Coincident(g95,g96)
    c: Equal(g6,g96)
    c: Parallel(g96,g6)
    c: Diameter(g97) = 6.35
    c: Coincident(g95,g98)
    c: Coincident(g97,g98)
    c: Equal(g6,g98)
    c: Parallel(g98,g6)
    c: Diameter(g99) = 6.35
    c: Coincident(g97,g100)
    c: Coincident(g99,g100)
    c: Equal(g6,g100)
    c: Parallel(g100,g6)
    c: Diameter(g101) = 6.35
    c: Coincident(g99,g102)
    c: Coincident(g101,g102)
    c: Equal(g6,g102)
    c: Parallel(g102,g6)
    c: Diameter(g103) = 6.35
    c: Coincident(g101,g104)
    c: Coincident(g103,g104)
    c: Equal(g6,g104)
    c: Parallel(g104,g6)
    c: Diameter(g105) = 6.35
    c: Coincident(g103,g106)
    c: Coincident(g105,g106)
    c: Equal(g6,g106)
    c: Parallel(g106,g6)
    c: Diameter(g107) = 6.35
    c: Coincident(g105,g108)
    c: Coincident(g107,g108)
    c: Equal(g6,g108)
    c: Parallel(g108,g6)
    c: Diameter(g109) = 6.35
    c: Coincident(g107,g110)
    c: Coincident(g109,g110)
    c: Equal(g6,g110)
    c: Parallel(g110,g6)
    c: Diameter(g111) = 6.35
    c: Coincident(g109,g112)
    c: Coincident(g111,g112)
    c: Equal(g6,g112)
    c: Parallel(g112,g6)
    c: Diameter(g113) = 6.35
    c: Coincident(g91,g114)
    c: Coincident(g113,g114)
    c: Equal(g26,g114)
    c: Perpendicular(g114,g6)
    c: Diameter(g115) = 6.35
    c: Coincident(g113,g116)
    c: Coincident(g115,g116)
    c: Equal(g6,g116)
    c: Parallel(g116,g6)
    c: Diameter(g117) = 6.35
    c: Coincident(g115,g118)
    c: Coincident(g117,g118)
    c: Equal(g6,g118)
    c: Parallel(g118,g6)
    c: Diameter(g119) = 6.35
    c: Coincident(g117,g120)
    c: Coincident(g119,g120)
    c: Equal(g6,g120)
    c: Parallel(g120,g6)
    c: Diameter(g121) = 6.35
    c: Coincident(g119,g122)
    c: Coincident(g121,g122)
    c: Equal(g6,g122)
    c: Parallel(g122,g6)
    c: Diameter(g123) = 6.35
    c: Coincident(g121,g124)
    c: Coincident(g123,g124)
    c: Equal(g6,g124)
    c: Parallel(g124,g6)
    c: Diameter(g125) = 6.35
    c: Coincident(g123,g126)
    c: Coincident(g125,g126)
    c: Equal(g6,g126)
    c: Parallel(g126,g6)
    c: Diameter(g127) = 6.35
    c: Coincident(g125,g128)
    c: Coincident(g127,g128)
    c: Equal(g6,g128)
    c: Parallel(g128,g6)
    c: Diameter(g129) = 6.35
    c: Coincident(g127,g130)
    c: Coincident(g129,g130)
    c: Equal(g6,g130)
    c: Parallel(g130,g6)
    c: Diameter(g131) = 6.35
    c: Coincident(g129,g132)
    c: Coincident(g131,g132)
    c: Equal(g6,g132)
    c: Parallel(g132,g6)
    c: Diameter(g133) = 6.35
    c: Coincident(g131,g134)
    c: Coincident(g133,g134)
    c: Equal(g6,g134)
    c: Parallel(g134,g6)
    c: Diameter(g135) = 6.35
    c: Coincident(g113,g136)
    c: Coincident(g135,g136)
    c: Equal(g26,g136)
    c: Perpendicular(g136,g6)
    c: Diameter(g137) = 6.35
    c: Coincident(g135,g138)
    c: Coincident(g137,g138)
    c: Equal(g6,g138)
    c: Parallel(g138,g6)
    c: Diameter(g139) = 6.35
    c: Coincident(g137,g140)
    c: Coincident(g139,g140)
    c: Equal(g6,g140)
    c: Parallel(g140,g6)
    c: Diameter(g141) = 6.35
    c: Coincident(g139,g142)
    c: Coincident(g141,g142)
    c: Equal(g6,g142)
    c: Parallel(g142,g6)
    c: Diameter(g143) = 6.35
    c: Coincident(g141,g144)
    c: Coincident(g143,g144)
    c: Equal(g6,g144)
    c: Parallel(g144,g6)
    c: Diameter(g145) = 6.35
    c: Coincident(g143,g146)
    c: Coincident(g145,g146)
    c: Equal(g6,g146)
    c: Parallel(g146,g6)
    c: Diameter(g147) = 6.35
    c: Coincident(g145,g148)
    c: Coincident(g147,g148)
    c: Equal(g6,g148)
    c: Parallel(g148,g6)
    c: Diameter(g149) = 6.35
    c: Coincident(g147,g150)
    c: Coincident(g149,g150)
    c: Equal(g6,g150)
    c: Parallel(g150,g6)
    c: Diameter(g151) = 6.35
    c: Coincident(g149,g152)
    c: Coincident(g151,g152)
    c: Equal(g6,g152)
    c: Parallel(g152,g6)
    c: Diameter(g153) = 6.35
    c: Coincident(g151,g154)
    c: Coincident(g153,g154)
    c: Equal(g6,g154)
    c: Parallel(g154,g6)
    c: Diameter(g155) = 6.35
    c: Coincident(g153,g156)
    c: Coincident(g155,g156)
    c: Equal(g6,g156)
    c: Parallel(g156,g6)
    c: Diameter(g157) = 6.35
    c: Coincident(g135,g158)
    c: Coincident(g157,g158)
    c: Equal(g26,g158)
    c: Perpendicular(g158,g6)
    c: Diameter(g159) = 6.35
    c: Coincident(g157,g160)
    c: Coincident(g159,g160)
    c: Equal(g6,g160)
    c: Parallel(g160,g6)
    c: Diameter(g161) = 6.35
    c: Coincident(g159,g162)
    c: Coincident(g161,g162)
    c: Equal(g6,g162)
    c: Parallel(g162,g6)
    c: Diameter(g163) = 6.35
    c: Coincident(g161,g164)
    c: Coincident(g163,g164)
    c: Equal(g6,g164)
    c: Parallel(g164,g6)
    c: Diameter(g165) = 6.35
    c: Coincident(g163,g166)
    c: Coincident(g165,g166)
    c: Equal(g6,g166)
    c: Parallel(g166,g6)
    c: Diameter(g167) = 6.35
    c: Coincident(g165,g168)
    c: Coincident(g167,g168)
    c: Equal(g6,g168)
    c: Parallel(g168,g6)
    c: Diameter(g169) = 6.35
    c: Coincident(g167,g170)
    c: Coincident(g169,g170)
    c: Equal(g6,g170)
    c: Parallel(g170,g6)
    c: Diameter(g171) = 6.35
    c: Coincident(g169,g172)
    c: Coincident(g171,g172)
    c: Equal(g6,g172)
    c: Parallel(g172,g6)
    c: Diameter(g173) = 6.35
    c: Coincident(g171,g174)
    c: Coincident(g173,g174)
    c: Equal(g6,g174)
    c: Parallel(g174,g6)
    c: Diameter(g175) = 6.35
    c: Coincident(g173,g176)
    c: Coincident(g175,g176)
    c: Equal(g6,g176)
    c: Parallel(g176,g6)
    c: Diameter(g177) = 6.35
    c: Coincident(g175,g178)
    c: Coincident(g177,g178)
    c: Equal(g6,g178)
    c: Parallel(g178,g6)
    c: Diameter(g179) = 6.35
    c: Coincident(g157,g180)
    c: Coincident(g179,g180)
    c: Equal(g26,g180)
    c: Perpendicular(g180,g6)
    c: Diameter(g181) = 6.35
    c: Coincident(g179,g182)
    c: Coincident(g181,g182)
    c: Equal(g6,g182)
    c: Parallel(g182,g6)
    c: Diameter(g183) = 6.35
    c: Coincident(g181,g184)
    c: Coincident(g183,g184)
    c: Equal(g6,g184)
    c: Parallel(g184,g6)
    c: Diameter(g185) = 6.35
    c: Coincident(g183,g186)
    c: Coincident(g185,g186)
    c: Equal(g6,g186)
    c: Parallel(g186,g6)
    c: Diameter(g187) = 6.35
    c: Coincident(g185,g188)
    c: Coincident(g187,g188)
    c: Equal(g6,g188)
    c: Parallel(g188,g6)
    c: Diameter(g189) = 6.35
    c: Coincident(g187,g190)
    c: Coincident(g189,g190)
    c: Equal(g6,g190)
    c: Parallel(g190,g6)
    c: Diameter(g191) = 6.35
    c: Coincident(g189,g192)
    c: Coincident(g191,g192)
    c: Equal(g6,g192)
    c: Parallel(g192,g6)
    c: Diameter(g193) = 6.35
    c: Coincident(g191,g194)
    c: Coincident(g193,g194)
    c: Equal(g6,g194)
    c: Parallel(g194,g6)
    c: Diameter(g195) = 6.35
    c: Coincident(g193,g196)
    c: Coincident(g195,g196)
    c: Equal(g6,g196)
    c: Parallel(g196,g6)
    c: Diameter(g197) = 6.35
    c: Coincident(g195,g198)
    c: Coincident(g197,g198)
    c: Equal(g6,g198)
    c: Parallel(g198,g6)
    c: Diameter(g199) = 6.35
    c: Coincident(g197,g200)
    c: Coincident(g199,g200)
    c: Equal(g6,g200)
    c: Parallel(g200,g6)
    c: Diameter(g201) = 6.35
    c: Coincident(g179,g202)
    c: Coincident(g201,g202)
    c: Equal(g26,g202)
    c: Perpendicular(g202,g6)
    c: Diameter(g203) = 6.35
    c: Coincident(g201,g204)
    c: Coincident(g203,g204)
    c: Equal(g6,g204)
    c: Parallel(g204,g6)
    c: Diameter(g205) = 6.35
    c: Coincident(g203,g206)
    c: Coincident(g205,g206)
    c: Equal(g6,g206)
    c: Parallel(g206,g6)
    c: Diameter(g207) = 6.35
    c: Coincident(g205,g208)
    c: Coincident(g207,g208)
    c: Equal(g6,g208)
    c: Parallel(g208,g6)
    c: Diameter(g209) = 6.35
    c: Coincident(g207,g210)
    c: Coincident(g209,g210)
    c: Equal(g6,g210)
    c: Parallel(g210,g6)
    c: Diameter(g211) = 6.35
    c: Coincident(g209,g212)
    c: Coincident(g211,g212)
    c: Equal(g6,g212)
    c: Parallel(g212,g6)
    c: Diameter(g213) = 6.35
    c: Coincident(g211,g214)
    c: Coincident(g213,g214)
    c: Equal(g6,g214)
    c: Parallel(g214,g6)
    c: Diameter(g215) = 6.35
    c: Coincident(g213,g216)
    c: Coincident(g215,g216)
    c: Equal(g6,g216)
    c: Parallel(g216,g6)
    c: Diameter(g217) = 6.35
    c: Coincident(g215,g218)
    c: Coincident(g217,g218)
    c: Equal(g6,g218)
    c: Parallel(g218,g6)
    c: Diameter(g219) = 6.35
    c: Coincident(g217,g220)
    c: Coincident(g219,g220)
    c: Equal(g6,g220)
    c: Parallel(g220,g6)
    c: Diameter(g221) = 6.35
    c: Coincident(g219,g222)
    c: Coincident(g221,g222)
    c: Equal(g6,g222)
    c: Parallel(g222,g6)
    c: Diameter(g223) = 6.35
    c: Coincident(g201,g224)
    c: Coincident(g223,g224)
    c: Equal(g26,g224)
    c: Perpendicular(g224,g6)
    c: Diameter(g225) = 6.35
    c: Coincident(g223,g226)
    c: Coincident(g225,g226)
    c: Equal(g6,g226)
    c: Parallel(g226,g6)
    c: Diameter(g227) = 6.35
    c: Coincident(g225,g228)
    c: Coincident(g227,g228)
    c: Equal(g6,g228)
    c: Parallel(g228,g6)
    c: Diameter(g229) = 6.35
    c: Coincident(g227,g230)
    c: Coincident(g229,g230)
    c: Equal(g6,g230)
    c: Parallel(g230,g6)
    c: Diameter(g231) = 6.35
    c: Coincident(g229,g232)
    c: Coincident(g231,g232)
    c: Equal(g6,g232)
    c: Parallel(g232,g6)
    c: Diameter(g233) = 6.35
    c: Coincident(g231,g234)
    c: Coincident(g233,g234)
    c: Equal(g6,g234)
    c: Parallel(g234,g6)
    c: Diameter(g235) = 6.35
    c: Coincident(g233,g236)
    c: Coincident(g235,g236)
    c: Equal(g6,g236)
    c: Parallel(g236,g6)
    c: Diameter(g237) = 6.35
    c: Coincident(g235,g238)
    c: Coincident(g237,g238)
    c: Equal(g6,g238)
    c: Parallel(g238,g6)
    c: Diameter(g239) = 6.35
    c: Coincident(g237,g240)
    c: Coincident(g239,g240)
    c: Equal(g6,g240)
    c: Parallel(g240,g6)
    c: Diameter(g241) = 6.35
    c: Coincident(g239,g242)
    c: Coincident(g241,g242)
    c: Equal(g6,g242)
    c: Parallel(g242,g6)
    c: Diameter(g243) = 6.35
    c: Coincident(g241,g244)
    c: Coincident(g243,g244)
    c: Equal(g6,g244)
    c: Parallel(g244,g6)
    c: Diameter(g245) = 6.35
    c: Coincident(g223,g246)
    c: Coincident(g245,g246)
    c: Equal(g26,g246)
    c: Perpendicular(g246,g6)
    c: Diameter(g247) = 6.35
    c: Coincident(g245,g248)
    c: Coincident(g247,g248)
    c: Equal(g6,g248)
    c: Parallel(g248,g6)
    c: Diameter(g249) = 6.35
    c: Coincident(g247,g250)
    c: Coincident(g249,g250)
    c: Equal(g6,g250)
    c: Parallel(g250,g6)
    c: Diameter(g251) = 6.35
    c: Coincident(g249,g252)
    c: Coincident(g251,g252)
    c: Equal(g6,g252)
    c: Parallel(g252,g6)
    c: Diameter(g253) = 6.35
    c: Coincident(g251,g254)
    c: Coincident(g253,g254)
    c: Equal(g6,g254)
    c: Parallel(g254,g6)
    c: Diameter(g255) = 6.35
    c: Coincident(g253,g256)
    c: Coincident(g255,g256)
    c: Equal(g6,g256)
    c: Parallel(g256,g6)
    c: Diameter(g257) = 6.35
    c: Coincident(g255,g258)
    c: Coincident(g257,g258)
    c: Equal(g6,g258)
    c: Parallel(g258,g6)
    c: Diameter(g259) = 6.35
    c: Coincident(g257,g260)
    c: Coincident(g259,g260)
    c: Equal(g6,g260)
    c: Parallel(g260,g6)
    c: Diameter(g261) = 6.35
    c: Coincident(g259,g262)
    c: Coincident(g261,g262)
    c: Equal(g6,g262)
    c: Parallel(g262,g6)
    c: Diameter(g263) = 6.35
    c: Coincident(g261,g264)
    c: Coincident(g263,g264)
    c: Equal(g6,g264)
    c: Parallel(g264,g6)
    c: Diameter(g265) = 6.35
    c: Coincident(g263,g266)
    c: Coincident(g265,g266)
    c: Equal(g6,g266)
    c: Parallel(g266,g6)
    c: Diameter(g267) = 6.35
    c: Coincident(g245,g268)
    c: Coincident(g267,g268)
    c: Equal(g26,g268)
    c: Perpendicular(g268,g6)
    c: Diameter(g269) = 6.35
    c: Coincident(g267,g270)
    c: Coincident(g269,g270)
    c: Equal(g6,g270)
    c: Parallel(g270,g6)
    c: Diameter(g271) = 6.35
    c: Coincident(g269,g272)
    c: Coincident(g271,g272)
    c: Equal(g6,g272)
    c: Parallel(g272,g6)
    c: Diameter(g273) = 6.35
    c: Coincident(g271,g274)
    c: Coincident(g273,g274)
    c: Equal(g6,g274)
    c: Parallel(g274,g6)
    c: Diameter(g275) = 6.35
    c: Coincident(g273,g276)
    c: Coincident(g275,g276)
    c: Equal(g6,g276)
    c: Parallel(g276,g6)
    c: Diameter(g277) = 6.35
    c: Coincident(g275,g278)
    c: Coincident(g277,g278)
    c: Equal(g6,g278)
    c: Parallel(g278,g6)
    c: Diameter(g279) = 6.35
    c: Coincident(g277,g280)
    c: Coincident(g279,g280)
    c: Equal(g6,g280)
    c: Parallel(g280,g6)
    c: Diameter(g281) = 6.35
    c: Coincident(g279,g282)
    c: Coincident(g281,g282)
    c: Equal(g6,g282)
    c: Parallel(g282,g6)
    c: Diameter(g283) = 6.35
    c: Coincident(g281,g284)
    c: Coincident(g283,g284)
    c: Equal(g6,g284)
    c: Parallel(g284,g6)
    c: Diameter(g285) = 6.35
    c: Coincident(g283,g286)
    c: Coincident(g285,g286)
    c: Equal(g6,g286)
    c: Parallel(g286,g6)
    c: Diameter(g287) = 6.35
    c: Coincident(g285,g288)
    c: Coincident(g287,g288)
    c: Equal(g6,g288)
    c: Parallel(g288,g6)
    c: Diameter(g289) = 6.35
    c: Coincident(g267,g290)
    c: Coincident(g289,g290)
    c: Equal(g26,g290)
    c: Perpendicular(g290,g6)
    c: Diameter(g291) = 6.35
    c: Coincident(g289,g292)
    c: Coincident(g291,g292)
    c: Equal(g6,g292)
    c: Parallel(g292,g6)
    c: Diameter(g293) = 6.35
    c: Coincident(g291,g294)
    c: Coincident(g293,g294)
    c: Equal(g6,g294)
    c: Parallel(g294,g6)
    c: Diameter(g295) = 6.35
    c: Coincident(g293,g296)
    c: Coincident(g295,g296)
    c: Equal(g6,g296)
    c: Parallel(g296,g6)
    c: Diameter(g297) = 6.35
    c: Coincident(g295,g298)
    c: Coincident(g297,g298)
    c: Equal(g6,g298)
    c: Parallel(g298,g6)
    c: Diameter(g299) = 6.35
    c: Coincident(g297,g300)
    c: Coincident(g299,g300)
    c: Equal(g6,g300)
    c: Parallel(g300,g6)
    c: Diameter(g301) = 6.35
    c: Coincident(g299,g302)
    c: Coincident(g301,g302)
    c: Equal(g6,g302)
    c: Parallel(g302,g6)
    c: Diameter(g303) = 6.35
    c: Coincident(g301,g304)
    c: Coincident(g303,g304)
    c: Equal(g6,g304)
    c: Parallel(g304,g6)
    c: Diameter(g305) = 6.35
    c: Coincident(g303,g306)
    c: Coincident(g305,g306)
    c: Equal(g6,g306)
    c: Parallel(g306,g6)
    c: Diameter(g307) = 6.35
    c: Coincident(g305,g308)
    c: Coincident(g307,g308)
    c: Equal(g6,g308)
    c: Parallel(g308,g6)
    c: Diameter(g309) = 6.35
    c: Coincident(g307,g310)
    c: Coincident(g309,g310)
    c: Equal(g6,g310)
    c: Parallel(g310,g6)
FEATURE [Part::Extrusion] Extrude
  Base = -> Sketch
  Dir = (0,0,1)
  DirMode = 2
  FaceMakerClass = Part::FaceMakerBullseye
  LengthFwd = 5.9944
  LengthRev = 0
  Solid = true
  Symmetric = false
FEATURE [TechDraw::DrawSVGTemplate] Template
  Height = 215.9
  Orientation = 1
  Width = 279.4
FEATURE [TechDraw::DrawProjGroupItem] ProjItem  label="Front"
  CoarseView = false
  Direction = (0,0,1)
  Focus = 100
  HardHidden = false
  IsoCount = 0
  IsoHidden = false
  IsoVisible = false
  LockPosition = true
  Perspective = false
  Rotation = 0
  RotationVector = (1,0,0)
  Scale = 0.2
  ScaleType = 2
  SeamHidden = false
  SeamVisible = true
  SmoothHidden = false
  SmoothVisible = true
  Source = -> [Extrude]
  Type = 0
  X = 0
  XDirection = (1,0,0)
  Y = 0
FEATURE [TechDraw::DrawProjGroupItem] ProjItem001  label="Left"
  CoarseView = false
  Direction = (-1,0,1e-16)
  Focus = 100
  HardHidden = false
  IsoCount = 0
  IsoHidden = false
  IsoVisible = false
  LockPosition = false
  Perspective = false
  Rotation = 0
  RotationVector = (1,0,0)
  Scale = 0.2
  ScaleType = 2
  SeamHidden = false
  SeamVisible = true
  SmoothHidden = false
  SmoothVisible = true
  Source = -> [Extrude]
  Type = 1
  X = 94.7412
  XDirection = (1e-16,0,1)
  Y = 0
FEATURE [TechDraw::DrawProjGroup] ProjGroup
  Anchor = -> ProjItem
  AutoDistribute = true
  LockPosition = false
  ProjectionType = 0
  Rotation = 0
  Scale = 0.2
  ScaleType = 2
  Source = -> [Extrude]
  Views = -> [ProjItem,ProjItem001]
  X = 138.639
  Y = 98.4003
  spacingX = 15.0114
  spacingY = 15.0114
FEATURE [TechDraw::DrawHatch] Hatch  label="HatchF0"
  HatchPattern = <path>
  Source = -> ProjItem [Face0]
FEATURE [TechDraw::DrawHatch] Hatch001  label="Hatch001F0"
  HatchPattern = <path>
  Source = -> ProjItem001 [Face0]
FEATURE [TechDraw::DrawViewDimension] Dimension
  Arbitrary = false
  ArbitraryTolerances = false
  EqualTolerance = true
  FormatSpec = %.3f
  FormatSpecOverTolerance = %+.3f
  FormatSpecUnderTolerance = %+.3f
  Inverted = false
  LockPosition = false
  MeasureType = 1
  OverTolerance = 0
  References2D = -> [ProjItem001]
  Rotation = 0
  ScaleType = 0
  TheoreticalExact = false
  Type = 1
  UnderTolerance = 0
  X = 23.4283
  Y = 60.3803
FEATURE [TechDraw::DrawViewDimension] Dimension001
  Arbitrary = false
  ArbitraryTolerances = false
  EqualTolerance = true
  FormatSpec = %.3f
  FormatSpecOverTolerance = %+.3f
  FormatSpecUnderTolerance = %+.3f
  Inverted = false
  LockPosition = false
  MeasureType = 1
  OverTolerance = 0
  References2D = -> [ProjItem]
  Rotation = 0
  ScaleType = 0
  TheoreticalExact = false
  Type = 2
  UnderTolerance = 0
  X = 71.1661
  Y = 0.697412
FEATURE [TechDraw::DrawViewDimension] Dimension002
  Arbitrary = false
  ArbitraryTolerances = false
  EqualTolerance = true
  FormatSpec = %.3f
  FormatSpecOverTolerance = %+.3f
  FormatSpecUnderTolerance = %+.3f
  Inverted = false
  LockPosition = false
  MeasureType = 1
  OverTolerance = 0
  References2D = -> [ProjItem]
  Rotation = 0
  ScaleType = 0
  TheoreticalExact = false
  Type = 1
  UnderTolerance = 0
  X = -0.280274
  Y = -83.7849
FEATURE [TechDraw::DrawViewDimension] Dimension003
  Arbitrary = false
  ArbitraryTolerances = false
  EqualTolerance = true
  FormatSpec = ⌀%.3f
  FormatSpecOverTolerance = %+.3f
  FormatSpecUnderTolerance = %+.3f
  Inverted = false
  LockPosition = false
  MeasureType = 1
  OverTolerance = 0
  References2D = -> [ProjItem]
  Rotation = 0
  ScaleType = 0
  TheoreticalExact = false
  Type = 5
  UnderTolerance = 0
  X = -65.5587
  Y = 89.3959
FEATURE [TechDraw::DrawViewDimension] Dimension004
  Arbitrary = false
  ArbitraryTolerances = false
  EqualTolerance = true
  FormatSpec = %.3f
  FormatSpecOverTolerance = %+.3f
  FormatSpecUnderTolerance = %+.3f
  Inverted = false
  LockPosition = false
  MeasureType = 1
  OverTolerance = 0
  References2D = -> [ProjItem]
  Rotation = 0
  ScaleType = 0
  TheoreticalExact = false
  Type = 2
  UnderTolerance = 0
  X = -41.0582
  Y = 92.2462
FEATURE [TechDraw::DrawViewDimension] Dimension005
  Arbitrary = false
  ArbitraryTolerances = false
  EqualTolerance = true
  FormatSpec = %.3f
  FormatSpecOverTolerance = %+.3f
  FormatSpecUnderTolerance = %+.3f
  Inverted = false
  LockPosition = false
  MeasureType = 1
  OverTolerance = 0
  References2D = -> [ProjItem]
  Rotation = 0
  ScaleType = 0
  TheoreticalExact = false
  Type = 1
  UnderTolerance = 0
  X = -76.1161
  Y = 56.7959
FEATURE [TechDraw::DrawViewDimension] Dimension006
  Arbitrary = false
  ArbitraryTolerances = false
  EqualTolerance = true
  FormatSpec = %.3f
  FormatSpecOverTolerance = %+.3f
  FormatSpecUnderTolerance = %+.3f
  Inverted = false
  LockPosition = false
  MeasureType = 1
  OverTolerance = 0
  References2D = -> [ProjItem]
  Rotation = 0
  ScaleType = 0
  TheoreticalExact = false
  Type = 2
  UnderTolerance = 0
  X = -27.1665
  Y = 92.8352
FEATURE [TechDraw::DrawViewDimension] Dimension007
  Arbitrary = false
  ArbitraryTolerances = false
  EqualTolerance = true
  FormatSpec = %.3f
  FormatSpecOverTolerance = %+.3f
  FormatSpecUnderTolerance = %+.3f
  Inverted = false
  LockPosition = false
  MeasureType = 1
  OverTolerance = 0
  References2D = -> [ProjItem]
  Rotation = 0
  ScaleType = 0
  TheoreticalExact = false
  Type = 1
  UnderTolerance = 0
  X = -76.3597
  Y = 35.8781
FEATURE [TechDraw::DrawViewAnnotation] Annotation
  Font = osifont
  LineSpace = 80
  LockPosition = false
  MaxWidth = -1
  Rotation = 0
  ScaleType = 0
  Text = repeat with equal spacing
  TextSize = 5.0038
  TextStyle = 0
  X = 150.712
  Y = 158.387
FEATURE [TechDraw::DrawViewAnnotation] Annotation001
  Font = osifont
  LineSpace = 80
  LockPosition = false
  MaxWidth = -1
  Rotation = 0
  ScaleType = 0
  Text = Figure S2 (Inverted 2) | Panel 6 [right side interior panel] | Quantity: 1
  TextSize = 5.0038
  TextStyle = 0
  X = 45.5819
  Y = 195.58
FEATURE [TechDraw::DrawViewAnnotation] Annotation003
  Font = osifont
  LineSpace = 80
  LockPosition = false
  MaxWidth = -1
  Rotation = 0
  ScaleType = 0
  Text = Units: Inches
  TextSize = 5.0038
  TextStyle = 0
  X = 259.08
  Y = 5.08
FEATURE [TechDraw::DrawPage] Page
  KeepUpdated = true
  NextBalloonIndex = 1
  ProjectionType = 0
  Template = -> Template
  Views = -> [ProjGroup,Dimension,Dimension001,Dimension002,Dimension003,Dimension004,Dimension005,Dimension006,Dimension007,Annotation,Annotation001,Annotation003]
note: 2 file-system paths scrubbed to <path> (originals preserved in the JSON sidecar)
